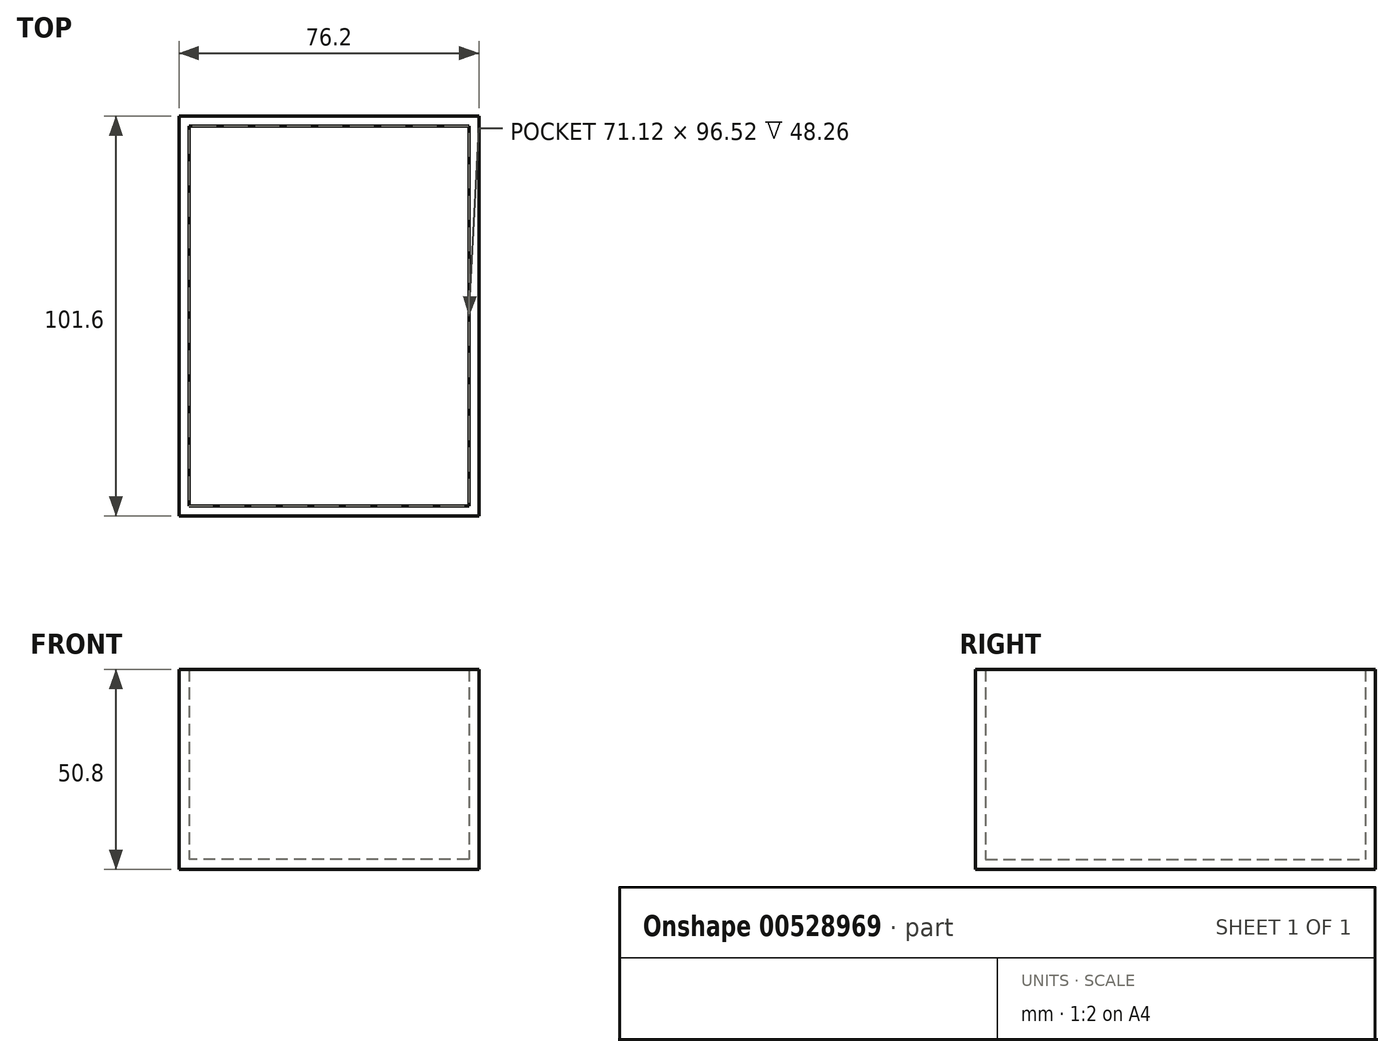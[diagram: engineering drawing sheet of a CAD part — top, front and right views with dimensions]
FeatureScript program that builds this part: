
annotation { "Feature Type Name" : "Feature", "Feature Type Description" : "" }
export const myFeature = defineFeature(function(context is Context, id is Id, definition is map)
    precondition{}
    {
        {
            var Q0;
            Q0=qCreatedBy(makeId("Top.planeOp"),FACE);
            var sketch = newSketch(context, id + "F0", { "sketchPlane" : qUnion([Q0])});
            skLineSegment(sketch, "E0.bottom", {"start": v(38.1, -50.8) * mm, "end": v(-38.1, -50.8) * mm});
            skLineSegment(sketch, "E0.top", {"start": v(38.1, 50.8) * mm, "end": v(-38.1, 50.8) * mm});
            skLineSegment(sketch, "E0.left", {"start": v(38.1, -50.8) * mm, "end": v(38.1, 50.8) * mm});
            skLineSegment(sketch, "E0.right", {"start": v(-38.1, -50.8) * mm, "end": v(-38.1, 50.8) * mm});
            skPoint(sketch, "E0.middle", {"position": v(0, 0) * mm});
            skSolve(sketch);
        }
        {
            var Q0;
            Q0 = qSketchRegion(id + "F0", true);
            extrude(context, id + "F1", {"entities" : qUnion([Q0]), "depth" : 25.4 * mm, "offsetDistance" : 25.4 * mm, "hasSecondDirection" : true, "secondDirectionOppositeDirection" : true, "secondDirectionDepth" : 25.4 * mm});
        }
        {
            var Q0;
            Q0=makeQuery(id+"F1.opExtrude","CAP_FACE",FACE,{"disambiguationData":[OSD([sQuery(id+"F0.wireOp",EDGE,"E0.bottom"),sQuery(id+"F0.wireOp",EDGE,"E0.top"),sQuery(id+"F0.wireOp",EDGE,"E0.left"),sQuery(id+"F0.wireOp",EDGE,"E0.right")])],"isStart":false});
            shell(context, id + "F2", {"entities" : qUnion([Q0]), "thickness" : 2.54 * mm});
        }
    });
